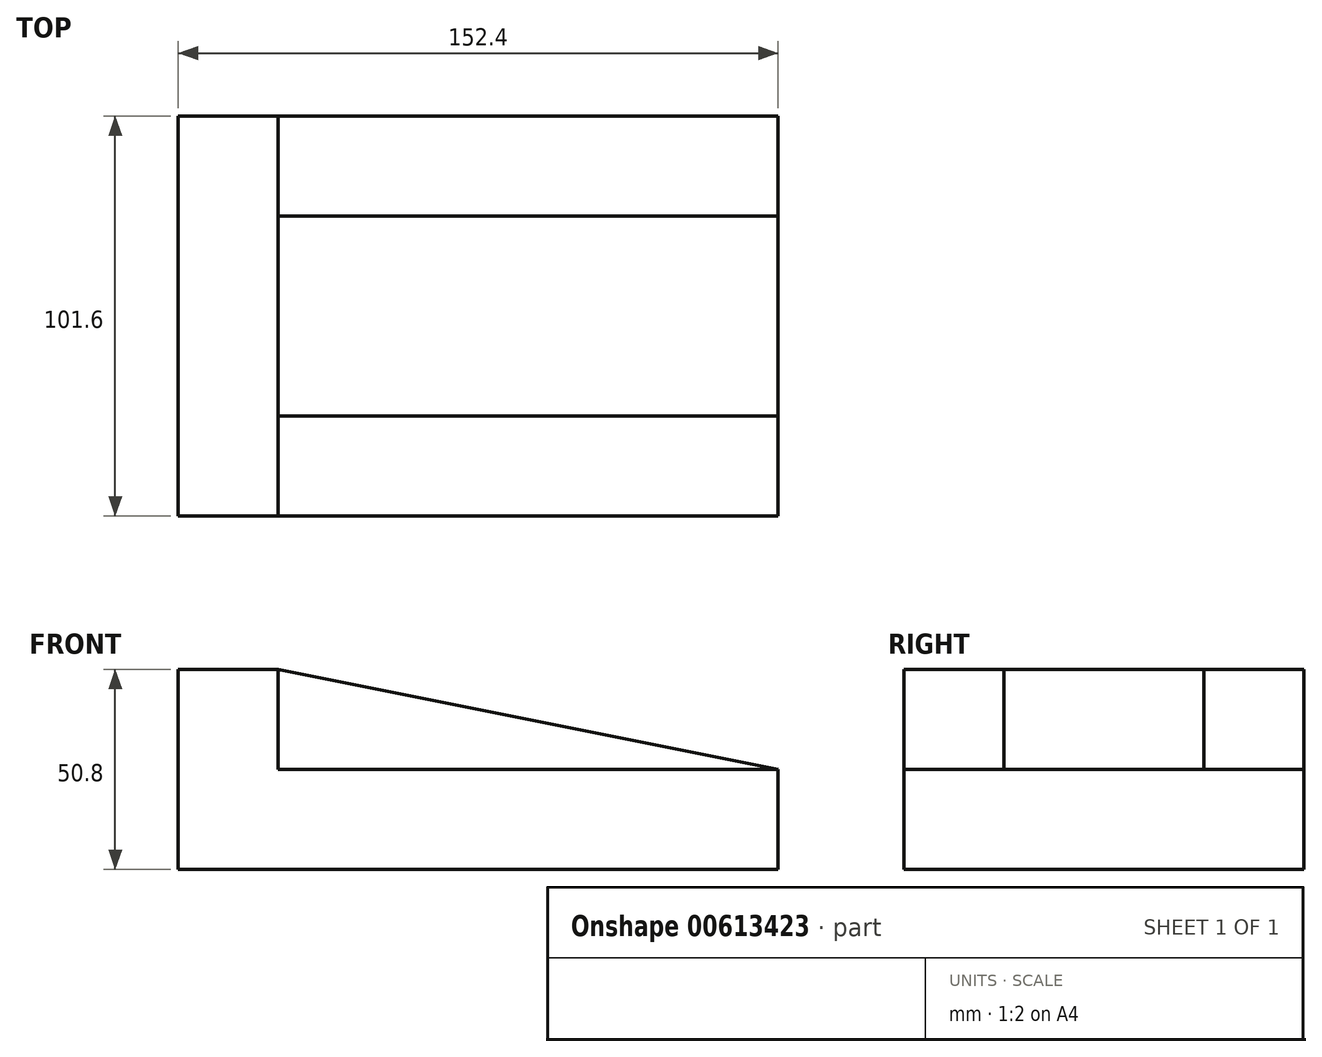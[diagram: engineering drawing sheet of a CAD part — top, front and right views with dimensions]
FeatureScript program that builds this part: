
annotation { "Feature Type Name" : "Feature", "Feature Type Description" : "" }
export const myFeature = defineFeature(function(context is Context, id is Id, definition is map)
    precondition{}
    {
        {
            var Q0;
            Q0=qCreatedBy(makeId("Front.planeOp"),FACE);
            var sketch = newSketch(context, id + "F0", { "sketchPlane" : qUnion([Q0])});
            skLineSegment(sketch, "E0", {"start": v(0, 0) * mm, "end": v(0, 50.8) * mm});
            skLineSegment(sketch, "E1", {"start": v(0, 50.8) * mm, "end": v(25.4, 50.8) * mm});
            skLineSegment(sketch, "E2", {"start": v(25.4, 50.8) * mm, "end": v(25.4, 25.4) * mm});
            skLineSegment(sketch, "E3", {"start": v(25.4, 25.4) * mm, "end": v(152.4, 25.4) * mm});
            skLineSegment(sketch, "E4", {"start": v(152.4, 25.4) * mm, "end": v(152.4, 0) * mm});
            skLineSegment(sketch, "E5", {"start": v(152.4, 0) * mm, "end": v(0, 0) * mm});
            skLineSegment(sketch, "E6", {"start": v(25.4, 50.8) * mm, "end": v(152.4, 25.4) * mm});
            skSolve(sketch);
        }
        {
            var Q0;
            Q0=makeQuery(id+"F0.imprint","IMPRINT",FACE,{"disambiguationData":[TD([[makeQuery(id+"F0.imprint","IMPRINT",EDGE,{"derivedFrom":sQuery(id+"F0.wireOp",EDGE,"E0")}),-1.0]])]});
            var Q1;
            Q1=makeQuery(id+"F0.imprint","IMPRINT",FACE,{"disambiguationData":[TD([[makeQuery(id+"F0.imprint","IMPRINT",EDGE,{"derivedFrom":sQuery(id+"F0.wireOp",EDGE,"E2")}),1.0]])]});
            extrude(context, id + "F1", {"entities" : qUnion([Q0, Q1]), "oppositeDirection" : true, "depth" : 101.6 * mm, "offsetDistance" : 25.4 * mm});
        }
        {
            var Q0;
            Q0=makeQuery(id+"F1.opExtrude","CAP_FACE",FACE,{"disambiguationData":[OSD([sQuery(id+"F0.wireOp",EDGE,"E0"),sQuery(id+"F0.wireOp",EDGE,"E1"),sQuery(id+"F0.wireOp",EDGE,"E4"),sQuery(id+"F0.wireOp",EDGE,"E5"),sQuery(id+"F0.wireOp",EDGE,"E6")])],"isStart":true});
            var sketch = newSketch(context, id + "F2", { "sketchPlane" : qUnion([Q0])});
            skLineSegment(sketch, "E7", {"start": v(25.4, 50.8) * mm, "end": v(25.4, 25.4) * mm});
            skLineSegment(sketch, "E8", {"start": v(25.4, 25.4) * mm, "end": v(152.4, 25.4) * mm});
            skSolve(sketch);
        }
        {
            var Q0;
            Q0 = qSketchRegion(id + "F2", true);
            var Q1;
            Q1=makeQuery(id+"F2.imprint","IMPRINT",FACE,{"disambiguationData":[TD([[makeQuery(id+"F2.imprint","IMPRINT",EDGE,{"derivedFrom":sQuery(id+"F2.wireOp",EDGE,"E7")}),1.0]])]});
            extrude(context, id + "F3", {"entities" : qUnion([Q0, Q1]), "operationType" : NewBodyOperationType.REMOVE, "oppositeDirection" : true, "depth" : 25.4 * mm, "offsetDistance" : 25.4 * mm});
        }
        {
            var Q0;
            Q0=makeQuery(id+"F1.opExtrude","CAP_FACE",FACE,{"disambiguationData":[OSD([sQuery(id+"F0.wireOp",EDGE,"E0"),sQuery(id+"F0.wireOp",EDGE,"E1"),sQuery(id+"F0.wireOp",EDGE,"E4"),sQuery(id+"F0.wireOp",EDGE,"E5"),sQuery(id+"F0.wireOp",EDGE,"E6")])],"isStart":false});
            var sketch = newSketch(context, id + "F4", { "sketchPlane" : qUnion([Q0])});
            skLineSegment(sketch, "E9", {"start": v(-25.4, 50.8) * mm, "end": v(-25.4, 25.4) * mm});
            skLineSegment(sketch, "E10", {"start": v(-25.4, 25.4) * mm, "end": v(-152.4, 25.4) * mm});
            skSolve(sketch);
        }
        {
            var Q0;
            Q0 = qSketchRegion(id + "F4", true);
            var Q1;
            Q1=makeQuery(id+"F4.imprint","IMPRINT",FACE,{"disambiguationData":[TD([[makeQuery(id+"F4.imprint","IMPRINT",EDGE,{"derivedFrom":sQuery(id+"F4.wireOp",EDGE,"E9")}),-1.0]])]});
            extrude(context, id + "F5", {"entities" : qUnion([Q0, Q1]), "operationType" : NewBodyOperationType.REMOVE, "oppositeDirection" : true, "depth" : 25.4 * mm, "offsetDistance" : 25.4 * mm});
        }
    });
